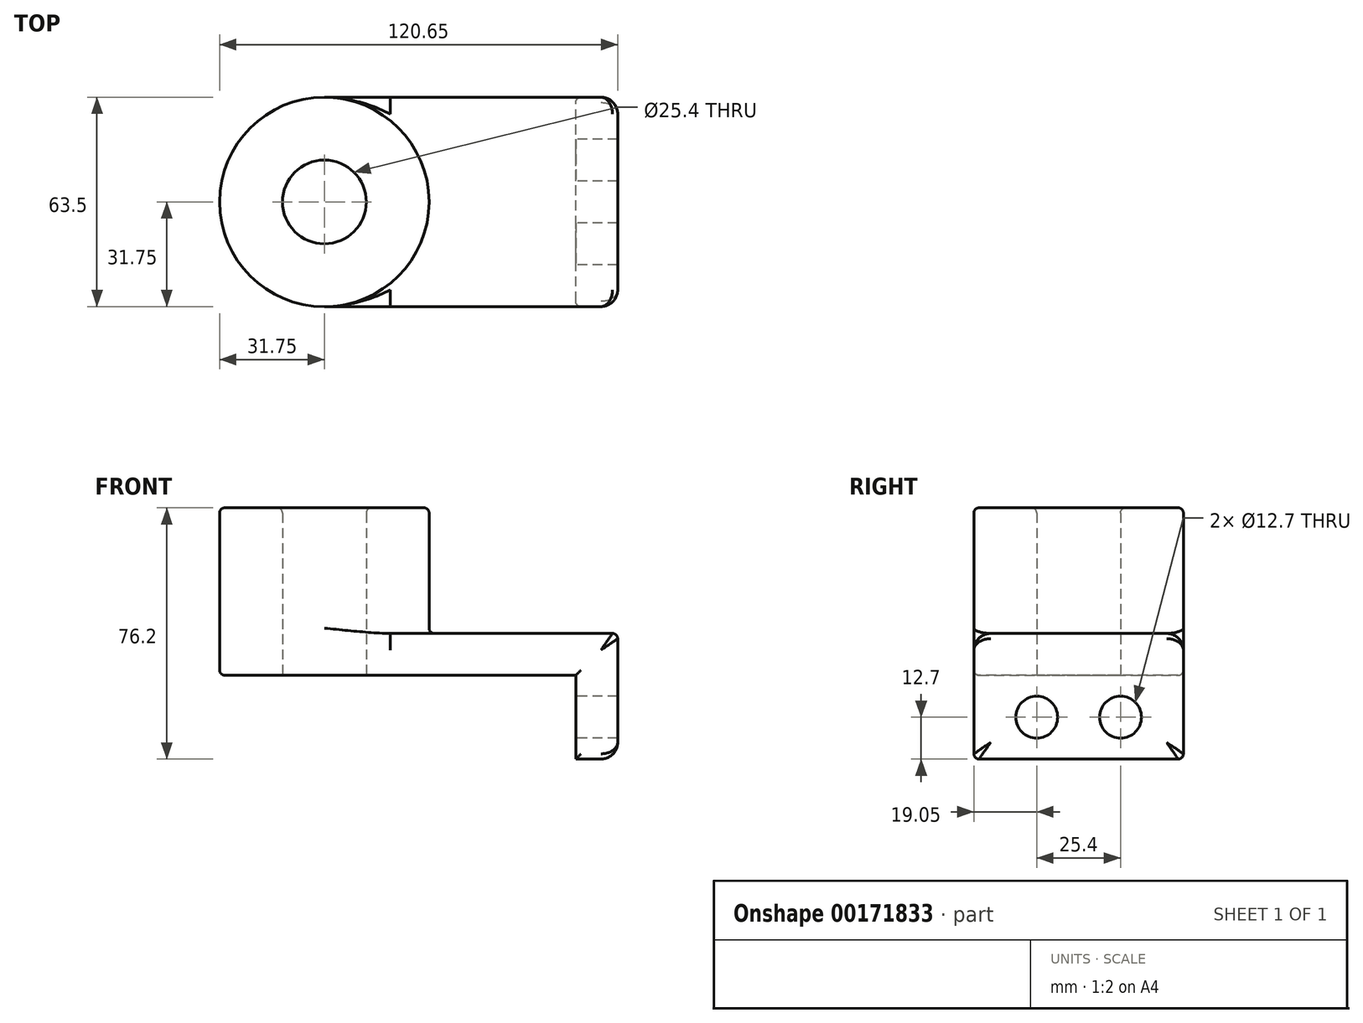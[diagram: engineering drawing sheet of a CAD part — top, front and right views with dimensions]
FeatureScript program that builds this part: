
annotation { "Feature Type Name" : "Feature", "Feature Type Description" : "" }
export const myFeature = defineFeature(function(context is Context, id is Id, definition is map)
    precondition{}
    {
        {
            var Q0;
            Q0=qCreatedBy(makeId("Top.planeOp"),FACE);
            var sketch = newSketch(context, id + "F0", { "sketchPlane" : qUnion([Q0])});
            skLineSegment(sketch, "E0.bottom", {"start": v(38.1, -31.75) * mm, "end": v(-38.1, -31.75) * mm});
            skLineSegment(sketch, "E0.top", {"start": v(38.1, 31.75) * mm, "end": v(-38.1, 31.75) * mm});
            skLineSegment(sketch, "E0.left", {"start": v(38.1, -31.75) * mm, "end": v(38.1, 31.75) * mm});
            skLineSegment(sketch, "E0.right", {"start": v(-38.1, -31.75) * mm, "end": v(-38.1, 31.75) * mm});
            skPoint(sketch, "E0.middle", {"position": v(0, 0) * mm});
            skCircle(sketch, "E1", {"center": v(-38.1, 0) * mm, "radius": 12.7 * mm});
            skCircle(sketch, "E2", {"center": v(-38.1, 0) * mm, "radius": 31.75 * mm});
            skSolve(sketch);
        }
        {
            var Q0;
            Q0 = qSketchRegion(id + "F0", true);
            extrude(context, id + "F1", {"entities" : qUnion([Q0]), "depth" : 12.7 * mm});
        }
        {
            var Q0;
            {var subQ1=sQuery(id+"F0.wireOp",EDGE,"E0.right");var subQ3=sQuery(id+"F0.wireOp",EDGE,"E1");var subQ4=makeQuery(id+"F0.imprint","INTERSECT",VERTEX,{"disambiguationData":[OD(0.0)],"derivedFrom":[subQ1,subQ3]});Q0=makeQuery(id+"F0.imprint","IMPRINT",FACE,{"disambiguationData":[TD([[makeQuery(id+"F0.imprint","IMPRINT",EDGE,{"disambiguationData":[TD([[subQ4,-1.0]])],"derivedFrom":subQ3}),-1.0]])]});}
            var Q1;
            {var subQ1=sQuery(id+"F0.wireOp",EDGE,"E0.right");var subQ3=sQuery(id+"F0.wireOp",EDGE,"E1");var subQ4=makeQuery(id+"F0.imprint","INTERSECT",VERTEX,{"disambiguationData":[OD(0.0)],"derivedFrom":[subQ1,subQ3]});Q1=makeQuery(id+"F0.imprint","IMPRINT",FACE,{"disambiguationData":[TD([[makeQuery(id+"F0.imprint","IMPRINT",EDGE,{"disambiguationData":[TD([[subQ4,1.0]])],"derivedFrom":subQ3}),-1.0]])]});}
            extrude(context, id + "F2", {"entities" : qUnion([Q0, Q1]), "operationType" : NewBodyOperationType.ADD, "depth" : 50.8 * mm});
        }
        {
            var Q0;
            Q0=makeQuery(id+"F1.opExtrude","SWEPT_FACE",FACE,{"disambiguationData":[OSD([sQuery(id+"F0.wireOp",EDGE,"E0.left")])]});
            var sketch = newSketch(context, id + "F3", { "sketchPlane" : qUnion([Q0])});
            skLineSegment(sketch, "E3.bottom", {"start": v(-31.75, 12.7) * mm, "end": v(31.75, 12.7) * mm});
            skLineSegment(sketch, "E3.top", {"start": v(-31.75, -25.4) * mm, "end": v(31.75, -25.4) * mm});
            skLineSegment(sketch, "E3.left", {"start": v(-31.75, 12.7) * mm, "end": v(-31.75, -25.4) * mm});
            skLineSegment(sketch, "E3.right", {"start": v(31.75, 12.7) * mm, "end": v(31.75, -25.4) * mm});
            skCircle(sketch, "E4", {"center": v(-12.7, -12.7) * mm, "radius": 6.35 * mm});
            skLineSegment(sketch, "E5", {"start": v(0, 0) * mm, "end": v(0, -25.4) * mm});
            skCircle(sketch, "E6", {"center": v(12.7, -12.7) * mm, "radius": 6.35 * mm});
            skSolve(sketch);
        }
        {
            var Q0;
            Q0 = qSketchRegion(id + "F3", true);
            extrude(context, id + "F4", {"entities" : qUnion([Q0]), "operationType" : NewBodyOperationType.ADD, "depth" : 12.7 * mm});
        }
        {
            var Q0;
            {var subQ0=sQuery(id+"F0.wireOp",EDGE,"E2");Q0=makeQuery(id+"F2.boolean.opBoolean","INTERSECT",EDGE,{"derivedFrom":[makeQuery(id+"F1.opExtrude","CAP_FACE",FACE,{"disambiguationData":[OSD([sQuery(id+"F0.wireOp",EDGE,"E0.bottom"),sQuery(id+"F0.wireOp",EDGE,"E0.top"),sQuery(id+"F0.wireOp",EDGE,"E0.left"),sQuery(id+"F0.wireOp",EDGE,"E1"),subQ0])],"isStart":false}),makeQuery(id+"F2.opExtrude","SWEPT_FACE",FACE,{"disambiguationData":[OSD([subQ0])]})]});}
            var Q1;
            Q1=makeQuery(id+"F4.opExtrude","CAP_EDGE",EDGE,{"disambiguationData":[OSD([sQuery(id+"F3.wireOp",EDGE,"E3.bottom")])],"isStart":false});
            var Q2;
            Q2=makeQuery(id+"F4.opExtrude","SWEPT_EDGE",EDGE,{"disambiguationData":[OSD([sQuery(id+"F3.wireOp",EDGE,"E3.top"),sQuery(id+"F3.wireOp",EDGE,"E3.right")])]});
            var Q3;
            Q3=makeQuery(id+"F4.opExtrude","SWEPT_EDGE",EDGE,{"disambiguationData":[OSD([sQuery(id+"F3.wireOp",EDGE,"E3.top"),sQuery(id+"F3.wireOp",EDGE,"E3.left")])]});
            var Q4;
            Q4=makeQuery(id+"F1.opExtrude","CAP_EDGE",EDGE,{"disambiguationData":[OSD([sQuery(id+"F0.wireOp",EDGE,"E0.bottom")])],"isStart":true});
            var Q5;
            Q5=makeQuery(id+"F4.opExtrude","CAP_EDGE",EDGE,{"disambiguationData":[OSD([sQuery(id+"F3.wireOp",EDGE,"E3.left")])],"isStart":true});
            var Q6;
            Q6=makeQuery(id+"F4.opExtrude","CAP_EDGE",EDGE,{"disambiguationData":[OSD([sQuery(id+"F3.wireOp",EDGE,"E3.right")])],"isStart":true});
            fillet(context, id + "F5", {"entities" : qUnion([Q0, Q1, Q2, Q3, Q4, Q5, Q6]), "radius" : 1.59 * mm, "tangentPropagation" : true, "allowEdgeOverflow" : false});
        }
        {
            var Q0;
            Q0=makeQuery(id+"F2.opExtrude","CAP_EDGE",EDGE,{"disambiguationData":[OSD([sQuery(id+"F0.wireOp",EDGE,"E2")])],"isStart":false});
            var Q1;
            Q1=makeQuery(id+"F2.opExtrude","CAP_EDGE",EDGE,{"disambiguationData":[OSD([sQuery(id+"F0.wireOp",EDGE,"E1")])],"isStart":false});
            fillet(context, id + "F6", {"entities" : qUnion([Q0, Q1]), "radius" : 1.59 * mm, "tangentPropagation" : true, "allowEdgeOverflow" : false});
        }
        {
            var Q0;
            Q0=makeQuery(id+"F4.boolean.opBoolean","MERGE",EDGE,{"derivedFrom":[makeQuery(id+"F1.opExtrude","CAP_EDGE",EDGE,{"disambiguationData":[OSD([sQuery(id+"F0.wireOp",EDGE,"E0.top")])],"isStart":false}),makeQuery(id+"F4.opExtrude","SWEPT_EDGE",EDGE,{"disambiguationData":[OSD([sQuery(id+"F3.wireOp",EDGE,"E3.bottom"),sQuery(id+"F3.wireOp",EDGE,"E3.right")])]})]});
            fillet(context, id + "F7", {"entities" : qUnion([Q0]), "radius" : 5.08 * mm, "tangentPropagation" : true, "allowEdgeOverflow" : false});
        }
    });
